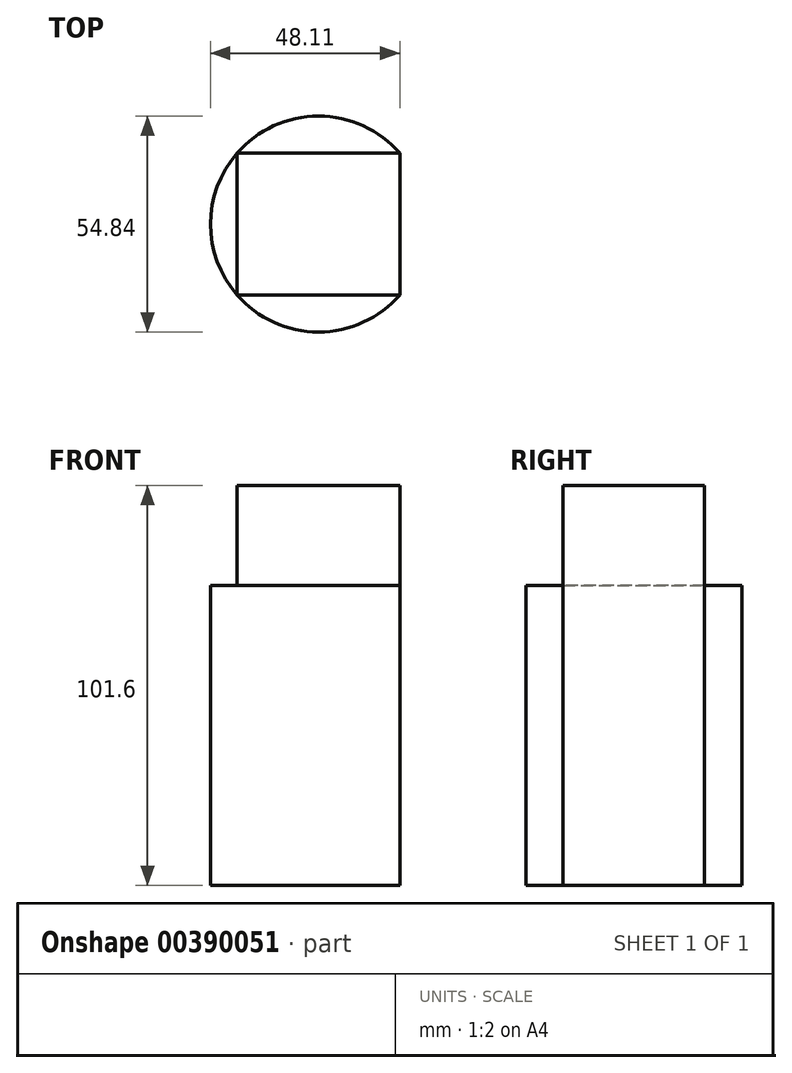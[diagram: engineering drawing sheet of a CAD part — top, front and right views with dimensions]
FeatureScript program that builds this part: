
annotation { "Feature Type Name" : "Feature", "Feature Type Description" : "" }
export const myFeature = defineFeature(function(context is Context, id is Id, definition is map)
    precondition{}
    {
        {
            var Q0;
            Q0=qCreatedBy(makeId("Top.planeOp"),FACE);
            var sketch = newSketch(context, id + "F0", { "sketchPlane" : qUnion([Q0])});
            skCircle(sketch, "E0", {"center": v(0, 0) * mm, "radius": 27.42 * mm});
            skLineSegment(sketch, "E1.bottom", {"start": v(20.69, -18) * mm, "end": v(-20.69, -18) * mm});
            skLineSegment(sketch, "E1.top", {"start": v(20.69, 18) * mm, "end": v(-20.69, 18) * mm});
            skLineSegment(sketch, "E1.left", {"start": v(20.69, -18) * mm, "end": v(20.69, 18) * mm});
            skLineSegment(sketch, "E1.right", {"start": v(-20.69, -18) * mm, "end": v(-20.69, 18) * mm});
            skSolve(sketch);
        }
        {
            var Q0;
            Q0=makeQuery(id+"F0.imprint","IMPRINT",FACE,{"disambiguationData":[TD([[makeQuery(id+"F0.imprint","IMPRINT",EDGE,{"derivedFrom":sQuery(id+"F0.wireOp",EDGE,"E1.bottom")}),-1.0]])]});
            extrude(context, id + "F1", {"entities" : qUnion([Q0]), "depth" : 101.6 * mm});
        }
        {
            var Q0;
            {var subQ0=sQuery(id+"F0.wireOp",EDGE,"E1.top");Q0=makeQuery(id+"F0.imprint","IMPRINT",FACE,{"disambiguationData":[TD([[makeQuery(id+"F0.imprint","IMPRINT",EDGE,{"derivedFrom":subQ0}),-1.0]])]});}
            var Q1;
            {var subQ0=sQuery(id+"F0.wireOp",EDGE,"E1.right");Q1=makeQuery(id+"F0.imprint","IMPRINT",FACE,{"disambiguationData":[TD([[makeQuery(id+"F0.imprint","IMPRINT",EDGE,{"derivedFrom":subQ0}),1.0]])]});}
            var Q2;
            {var subQ0=sQuery(id+"F0.wireOp",EDGE,"E1.bottom");Q2=makeQuery(id+"F0.imprint","IMPRINT",FACE,{"disambiguationData":[TD([[makeQuery(id+"F0.imprint","IMPRINT",EDGE,{"derivedFrom":subQ0}),1.0]])]});}
            extrude(context, id + "F2", {"entities" : qUnion([Q0, Q1, Q2]), "operationType" : NewBodyOperationType.ADD, "depth" : 76.2 * mm});
        }
    });
